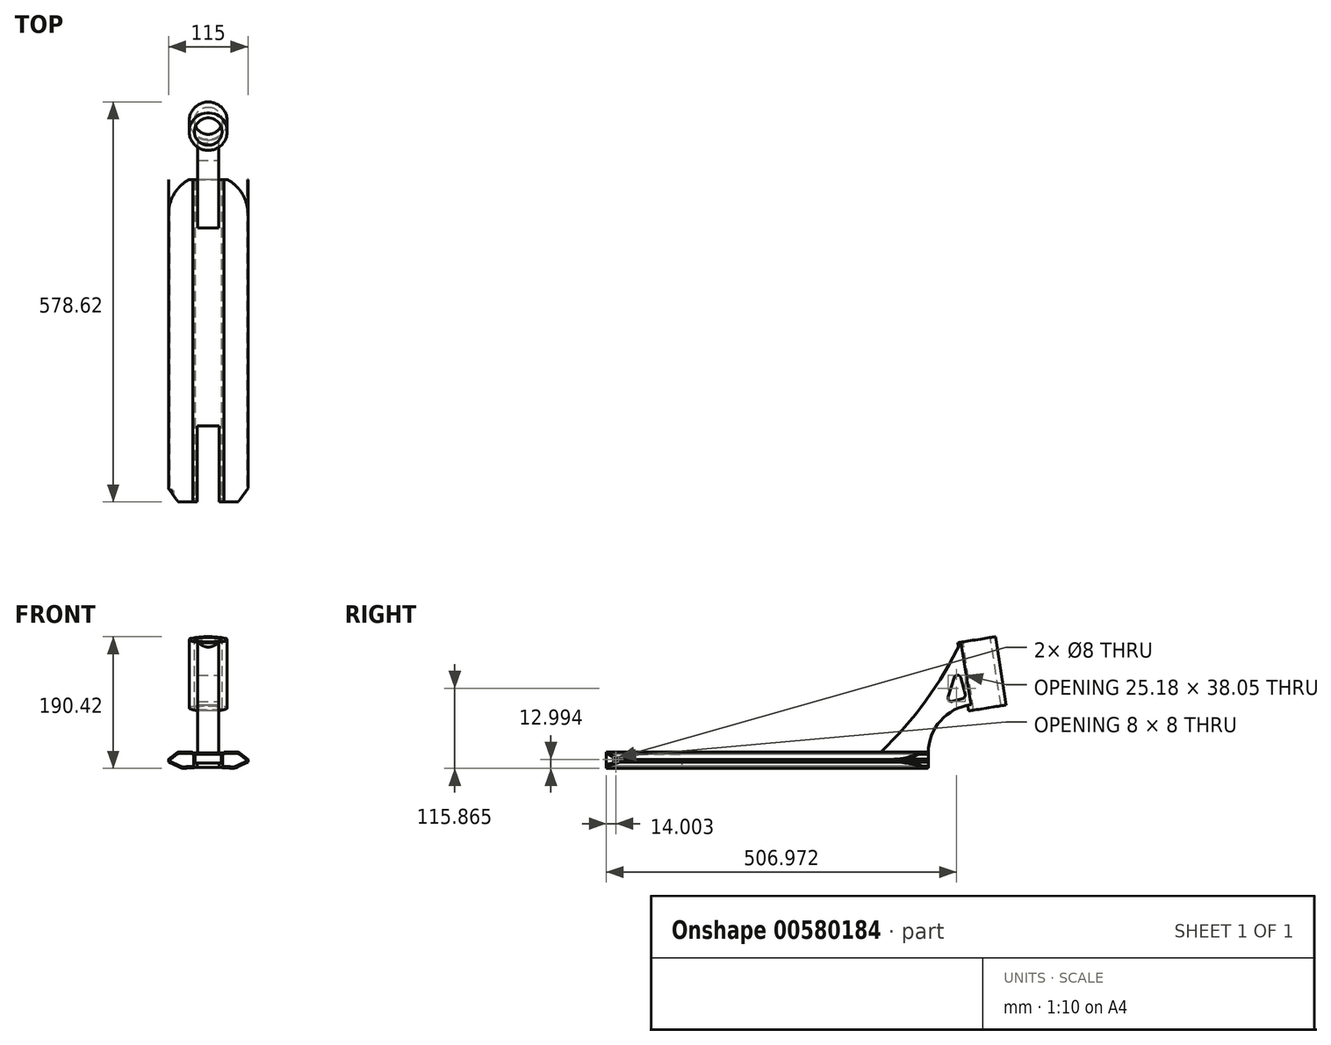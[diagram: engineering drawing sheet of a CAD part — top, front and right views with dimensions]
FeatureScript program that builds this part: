
annotation { "Feature Type Name" : "Feature", "Feature Type Description" : "" }
export const myFeature = defineFeature(function(context is Context, id is Id, definition is map)
    precondition{}
    {
        {
            var Q0;
            Q0=qCreatedBy(makeId("Front.planeOp"),FACE);
            var sketch = newSketch(context, id + "F0", { "sketchPlane" : qUnion([Q0])});
            skLineSegment(sketch, "E0", {"start": v(0, 0) * mm, "end": v(0, 62.93) * mm, "construction": true});
            skLineSegment(sketch, "E1", {"start": v(0, 21.56) * mm, "end": v(22.5, 21.56) * mm});
            skLineSegment(sketch, "E2", {"start": v(22.5, 21.56) * mm, "end": v(22.5, 22.86) * mm});
            skLineSegment(sketch, "E3", {"start": v(22.5, 22.86) * mm, "end": v(43.82, 22.86) * mm});
            skLineSegment(sketch, "E4", {"start": v(43.82, 22.86) * mm, "end": v(57.5, 12.15) * mm});
            skLineSegment(sketch, "E5", {"start": v(57.5, 12.15) * mm, "end": v(57.5, 8.15) * mm});
            skLineSegment(sketch, "E6", {"start": v(57.5, 8.15) * mm, "end": v(37.5, -1.14) * mm});
            skLineSegment(sketch, "E7.MirrorCS", {"start": v(0, 21.56) * mm, "end": v(-22.5, 21.56) * mm});
            skLineSegment(sketch, "E8.MirrorCS", {"start": v(-22.5, 21.56) * mm, "end": v(-22.5, 22.86) * mm});
            skLineSegment(sketch, "E9.MirrorCS", {"start": v(-22.5, 22.86) * mm, "end": v(-43.82, 22.86) * mm});
            skLineSegment(sketch, "E10.MirrorCS", {"start": v(-43.82, 22.86) * mm, "end": v(-57.5, 12.15) * mm});
            skLineSegment(sketch, "E11.MirrorCS", {"start": v(-57.5, 8.15) * mm, "end": v(-37.5, -1.14) * mm});
            skLineSegment(sketch, "E12.MirrorCS", {"start": v(-57.5, 12.15) * mm, "end": v(-57.5, 8.15) * mm});
            skArc(sketch, "E13", {"start": v(37.5, -1.14) * mm, "mid": v(0, 0.56) * mm, "end": v(-37.5, -1.14) * mm});
            skSolve(sketch);
        }
        {
            var Q0;
            Q0 = qSketchRegion(id + "F0", true);
            extrude(context, id + "F1", {"entities" : qUnion([Q0]), "endBound" : BoundingType.SYMMETRIC, "depth" : 500 * mm, "offsetDistance" : 25 * mm});
        }
        {
            var Q0;
            Q0=qCreatedBy(makeId("Front.planeOp"),FACE);
            var sketch = newSketch(context, id + "F2", { "sketchPlane" : qUnion([Q0])});
            skLineSegment(sketch, "E14.bottom", {"start": v(-19, 19.56) * mm, "end": v(19, 19.56) * mm});
            skLineSegment(sketch, "E14.top", {"start": v(-19, 6.56) * mm, "end": v(19, 6.56) * mm});
            skLineSegment(sketch, "E14.left", {"start": v(-19, 19.56) * mm, "end": v(-19, 6.56) * mm});
            skLineSegment(sketch, "E14.right", {"start": v(19, 19.56) * mm, "end": v(19, 6.56) * mm});
            skSolve(sketch);
        }
        {
            var Q0;
            Q0 = qSketchRegion(id + "F2", true);
            extrude(context, id + "F3", {"entities" : qUnion([Q0]), "operationType" : NewBodyOperationType.REMOVE, "endBound" : BoundingType.SYMMETRIC, "oppositeDirection" : true, "depth" : 500 * mm, "offsetDistance" : 25 * mm});
        }
        {
            var Q0;
            Q0=makeQuery(id+"F1.opExtrude","SWEPT_EDGE",EDGE,{"disambiguationData":[OSD([sQuery(id+"F0.wireOp",EDGE,"E8.MirrorCS"),sQuery(id+"F0.wireOp",EDGE,"E9.MirrorCS")])]});
            var Q1;
            Q1=makeQuery(id+"F1.opExtrude","SWEPT_EDGE",EDGE,{"disambiguationData":[OSD([sQuery(id+"F0.wireOp",EDGE,"E2"),sQuery(id+"F0.wireOp",EDGE,"E3")])]});
            fillet(context, id + "F4", {"entities" : qUnion([Q0, Q1]), "radius" : 2 * mm, "tangentPropagation" : true, "allowEdgeOverflow" : false});
        }
        {
            var Q0;
            Q0=makeQuery(id+"F1.opExtrude","SWEPT_EDGE",EDGE,{"disambiguationData":[OSD([sQuery(id+"F0.wireOp",EDGE,"E3"),sQuery(id+"F0.wireOp",EDGE,"E4")])]});
            var Q1;
            Q1=makeQuery(id+"F1.opExtrude","SWEPT_EDGE",EDGE,{"disambiguationData":[OSD([sQuery(id+"F0.wireOp",EDGE,"E9.MirrorCS"),sQuery(id+"F0.wireOp",EDGE,"E10.MirrorCS")])]});
            var Q2;
            Q2=makeQuery(id+"F1.opExtrude","SWEPT_EDGE",EDGE,{"disambiguationData":[OSD([sQuery(id+"F0.wireOp",EDGE,"E11.MirrorCS"),sQuery(id+"F0.wireOp",EDGE,"E13")])]});
            var Q3;
            Q3=makeQuery(id+"F1.opExtrude","SWEPT_EDGE",EDGE,{"disambiguationData":[OSD([sQuery(id+"F0.wireOp",EDGE,"E6"),sQuery(id+"F0.wireOp",EDGE,"E13")])]});
            fillet(context, id + "F5", {"entities" : qUnion([Q0, Q1, Q2, Q3]), "radius" : 9 * mm, "tangentPropagation" : true, "allowEdgeOverflow" : false});
        }
        {
            var Q0;
            Q0=makeQuery(id+"F1.opExtrude","CAP_FACE",FACE,{"disambiguationData":[OSD([sQuery(id+"F0.wireOp",EDGE,"E1"),sQuery(id+"F0.wireOp",EDGE,"E2"),sQuery(id+"F0.wireOp",EDGE,"E3"),sQuery(id+"F0.wireOp",EDGE,"E4"),sQuery(id+"F0.wireOp",EDGE,"E5"),sQuery(id+"F0.wireOp",EDGE,"E6"),sQuery(id+"F0.wireOp",EDGE,"E7.MirrorCS"),sQuery(id+"F0.wireOp",EDGE,"E8.MirrorCS"),sQuery(id+"F0.wireOp",EDGE,"E9.MirrorCS"),sQuery(id+"F0.wireOp",EDGE,"E10.MirrorCS"),sQuery(id+"F0.wireOp",EDGE,"E11.MirrorCS"),sQuery(id+"F0.wireOp",EDGE,"E12.MirrorCS"),sQuery(id+"F0.wireOp",EDGE,"E13")])],"isStart":false});
            var sketch = newSketch(context, id + "F6", { "sketchPlane" : qUnion([Q0])});
            skLineSegment(sketch, "E15.0.0", {"start": v(-57.5, 8.15) * mm, "end": v(-39.68, -0.12) * mm});
            skArc(sketch, "E15.0.1", {"start": v(-39.68, -0.12) * mm, "mid": v(-37.46, -0.82) * mm, "end": v(-35.13, -0.93) * mm});
            skArc(sketch, "E15.0.2", {"start": v(-35.13, -0.93) * mm, "mid": v(0, 0.56) * mm, "end": v(35.13, -0.93) * mm});
            skArc(sketch, "E15.0.3", {"start": v(35.13, -0.93) * mm, "mid": v(37.46, -0.82) * mm, "end": v(39.68, -0.12) * mm});
            skLineSegment(sketch, "E15.0.4", {"start": v(39.68, -0.12) * mm, "end": v(57.5, 8.15) * mm});
            skLineSegment(sketch, "E15.0.5", {"start": v(57.5, 8.15) * mm, "end": v(57.5, 12.15) * mm});
            skLineSegment(sketch, "E15.0.6", {"start": v(57.5, 12.15) * mm, "end": v(46.27, 20.95) * mm});
            skArc(sketch, "E15.0.7", {"start": v(46.27, 20.95) * mm, "mid": v(43.65, 22.37) * mm, "end": v(40.72, 22.86) * mm});
            skLineSegment(sketch, "E15.0.8", {"start": v(40.72, 22.86) * mm, "end": v(24.37, 22.86) * mm});
            skArc(sketch, "E15.0.9", {"start": v(24.37, 22.86) * mm, "mid": v(23.23, 22.5) * mm, "end": v(22.5, 21.56) * mm});
            skLineSegment(sketch, "E15.0.10", {"start": v(22.5, 21.56) * mm, "end": v(-22.5, 21.56) * mm});
            skArc(sketch, "E15.0.11", {"start": v(-22.5, 21.56) * mm, "mid": v(-23.23, 22.5) * mm, "end": v(-24.37, 22.86) * mm});
            skLineSegment(sketch, "E15.0.12", {"start": v(-24.37, 22.86) * mm, "end": v(-40.72, 22.86) * mm});
            skArc(sketch, "E15.0.13", {"start": v(-40.72, 22.86) * mm, "mid": v(-43.65, 22.37) * mm, "end": v(-46.27, 20.95) * mm});
            skLineSegment(sketch, "E15.0.14", {"start": v(-46.27, 20.95) * mm, "end": v(-57.5, 12.15) * mm});
            skLineSegment(sketch, "E15.0.15", {"start": v(-57.5, 12.15) * mm, "end": v(-57.5, 8.15) * mm});
            skArc(sketch, "E16.0", {"start": v(-35.3, 1.07) * mm, "mid": v(0, 2.56) * mm, "end": v(35.3, 1.07) * mm});
            skArc(sketch, "E16.1", {"start": v(-38.84, 1.7) * mm, "mid": v(-37.1, 1.15) * mm, "end": v(-35.3, 1.07) * mm});
            skLineSegment(sketch, "E16.2", {"start": v(-24.87, 20.86) * mm, "end": v(-40.72, 20.86) * mm});
            skArc(sketch, "E16.3", {"start": v(-40.72, 20.86) * mm, "mid": v(-43, 20.48) * mm, "end": v(-45.03, 19.38) * mm});
            skLineSegment(sketch, "E16.4", {"start": v(-45.03, 19.38) * mm, "end": v(-55.62, 11.09) * mm});
            skLineSegment(sketch, "E16.5", {"start": v(-55.42, 9.4) * mm, "end": v(-38.84, 1.7) * mm});
            skPoint(sketch, "E17.visualSharp", {"position": v(-56.9, 10.08) * mm});
            skArc(sketch, "E17.filletArc", {"start": v(-55.62, 11.09) * mm, "mid": v(-56, 10.18) * mm, "end": v(-55.42, 9.4) * mm});
            skLineSegment(sketch, "E18", {"start": v(-21, 2.03) * mm, "end": v(-21, 19.56) * mm});
            skLineSegment(sketch, "E19", {"start": v(-21, 19.56) * mm, "end": v(-23, 19.56) * mm});
            skPoint(sketch, "E20.visualSharp", {"position": v(-26.02, 20.86) * mm});
            skArc(sketch, "E20.filletArc", {"start": v(-23, 19.56) * mm, "mid": v(-23.73, 20.5) * mm, "end": v(-24.87, 20.86) * mm});
            skLineSegment(sketch, "E21.MirrorCS", {"start": v(21, 2.03) * mm, "end": v(21, 19.56) * mm});
            skLineSegment(sketch, "E22.MirrorCS", {"start": v(21, 19.56) * mm, "end": v(23, 19.56) * mm});
            skArc(sketch, "E23.MirrorCS", {"start": v(23, 19.56) * mm, "mid": v(23.73, 20.5) * mm, "end": v(24.87, 20.86) * mm});
            skLineSegment(sketch, "E24.MirrorCS", {"start": v(24.87, 20.86) * mm, "end": v(40.72, 20.86) * mm});
            skArc(sketch, "E25.MirrorCS", {"start": v(40.72, 20.86) * mm, "mid": v(43, 20.48) * mm, "end": v(45.03, 19.38) * mm});
            skLineSegment(sketch, "E26.MirrorCS", {"start": v(45.03, 19.38) * mm, "end": v(55.62, 11.09) * mm});
            skArc(sketch, "E27.MirrorCS", {"start": v(55.62, 11.09) * mm, "mid": v(56, 10.18) * mm, "end": v(55.42, 9.4) * mm});
            skLineSegment(sketch, "E28.MirrorCS", {"start": v(55.42, 9.4) * mm, "end": v(38.84, 1.7) * mm});
            skArc(sketch, "E29.MirrorCS", {"start": v(38.84, 1.7) * mm, "mid": v(37.1, 1.15) * mm, "end": v(35.3, 1.07) * mm});
            skSolve(sketch);
        }
        {
            var Q0;
            {var subQ0=sQuery(id+"F6.wireOp",EDGE,"E16.1");Q0=makeQuery(id+"F6.imprint","IMPRINT",FACE,{"disambiguationData":[TD([[makeQuery(id+"F6.imprint","IMPRINT",EDGE,{"derivedFrom":subQ0}),1.0]])]});}
            var Q1;
            {var subQ2=sQuery(id+"F6.wireOp",EDGE,"E21.MirrorCS");Q1=makeQuery(id+"F6.imprint","IMPRINT",FACE,{"disambiguationData":[TD([[makeQuery(id+"F6.imprint","IMPRINT",EDGE,{"derivedFrom":subQ2}),-1.0]])]});}
            extrude(context, id + "F7", {"entities" : qUnion([Q0, Q1]), "operationType" : NewBodyOperationType.REMOVE, "endBound" : BoundingType.THROUGH_ALL, "oppositeDirection" : true, "depth" : 25 * mm, "offsetDistance" : 25 * mm});
        }
        {
            var Q0;
            Q0=qCreatedBy(makeId("Top.planeOp"),FACE);
            var sketch = newSketch(context, id + "F8", { "sketchPlane" : qUnion([Q0])});
            skArc(sketch, "E30", {"start": v(57.5, 200.38) * mm, "mid": v(0, 257.5) * mm, "end": v(-57.5, 200.38) * mm});
            skLineSegment(sketch, "E31", {"start": v(-57.5, 200.38) * mm, "end": v(-56.97, 280.38) * mm});
            skLineSegment(sketch, "E32", {"start": v(57.5, 200.38) * mm, "end": v(56.97, 280.38) * mm});
            skLineSegment(sketch, "E33", {"start": v(56.97, 280.38) * mm, "end": v(-56.97, 280.38) * mm});
            skSolve(sketch);
        }
        {
            var Q0;
            Q0 = qSketchRegion(id + "F8", true);
            extrude(context, id + "F9", {"entities" : qUnion([Q0]), "operationType" : NewBodyOperationType.REMOVE, "endBound" : BoundingType.THROUGH_ALL, "oppositeDirection" : true, "depth" : 25 * mm, "offsetDistance" : 25 * mm, "hasSecondDirection" : true, "secondDirectionBound" : SecondDirectionBoundingType.THROUGH_ALL, "secondDirectionOppositeDirection" : false, "secondDirectionDepth" : 25 * mm});
        }
        {
            var Q0;
            Q0=qCreatedBy(makeId("Top.planeOp"),FACE);
            var sketch = newSketch(context, id + "F10", { "sketchPlane" : qUnion([Q0])});
            skLineSegment(sketch, "E34", {"start": v(-43.3, -216.07) * mm, "end": v(-16, -216.07) * mm});
            skLineSegment(sketch, "E35", {"start": v(-16, -216.07) * mm, "end": v(-16, -106.07) * mm});
            skLineSegment(sketch, "E36", {"start": v(-16, -106.07) * mm, "end": v(16, -106.07) * mm});
            skLineSegment(sketch, "E37", {"start": v(16, -106.07) * mm, "end": v(16, -216.07) * mm});
            skLineSegment(sketch, "E38", {"start": v(16, -216.07) * mm, "end": v(43.3, -216.07) * mm});
            skLineSegment(sketch, "E39", {"start": v(43.3, -216.07) * mm, "end": v(68, -182.07) * mm});
            skLineSegment(sketch, "E40", {"start": v(68, -182.07) * mm, "end": v(68, -312.07) * mm});
            skLineSegment(sketch, "E41", {"start": v(68, -312.07) * mm, "end": v(-68, -312.07) * mm});
            skLineSegment(sketch, "E42", {"start": v(-68, -312.07) * mm, "end": v(-68, -182.07) * mm});
            skLineSegment(sketch, "E43", {"start": v(-68, -182.07) * mm, "end": v(-43.3, -216.07) * mm});
            skLineSegment(sketch, "E44", {"start": v(0, 0) * mm, "end": v(0, -312.07) * mm});
            skPoint(sketch, "E44.endSnap0", {"position": v(0, -312.07) * mm});
            skSolve(sketch);
        }
        {
            var Q0;
            Q0 = qSketchRegion(id + "F10", true);
            extrude(context, id + "F11", {"entities" : qUnion([Q0]), "operationType" : NewBodyOperationType.REMOVE, "endBound" : BoundingType.THROUGH_ALL, "oppositeDirection" : true, "depth" : 25 * mm, "offsetDistance" : 25 * mm, "hasSecondDirection" : true, "secondDirectionBound" : SecondDirectionBoundingType.THROUGH_ALL, "secondDirectionOppositeDirection" : false, "secondDirectionDepth" : 25 * mm});
        }
        {
            var Q0;
            Q0=qCreatedBy(makeId("Right.planeOp"),FACE);
            var sketch = newSketch(context, id + "F12", { "sketchPlane" : qUnion([Q0])});
            skLineSegment(sketch, "E45", {"start": v(180, 21.56) * mm, "end": v(250, 21.56) * mm});
            skArc(sketch, "E46", {"start": v(311.37, 91.03) * mm, "mid": v(267.54, 67.9) * mm, "end": v(250, 21.56) * mm});
            skArc(sketch, "E47", {"start": v(180, 21.56) * mm, "mid": v(245.78, 96.25) * mm, "end": v(297.03, 181.56) * mm});
            skLineSegment(sketch, "E48", {"start": v(297.03, 181.56) * mm, "end": v(342.46, 188.76) * mm});
            skLineSegment(sketch, "E49", {"start": v(342.46, 188.76) * mm, "end": v(358.1, 90) * mm});
            skLineSegment(sketch, "E50", {"start": v(358.1, 90) * mm, "end": v(312.67, 82.8) * mm});
            skLineSegment(sketch, "E51", {"start": v(311.37, 91.03) * mm, "end": v(312.67, 82.8) * mm});
            skSolve(sketch);
        }
        {
            var Q0;
            Q0 = qSketchRegion(id + "F12", true);
            extrude(context, id + "F13", {"entities" : qUnion([Q0]), "operationType" : NewBodyOperationType.ADD, "endBound" : BoundingType.SYMMETRIC, "depth" : 30 * mm, "offsetDistance" : 25 * mm});
        }
        {
            var Q0;
            Q0=makeQuery(id+"F13.opExtrude","SWEPT_FACE",FACE,{"disambiguationData":[OSD([sQuery(id+"F12.wireOp",EDGE,"E48")])]});
            var sketch = newSketch(context, id + "F14", { "sketchPlane" : qUnion([Q0])});
            skCircle(sketch, "E52", {"center": v(0, 344.78) * mm, "radius": 27.5 * mm});
            skSolve(sketch);
        }
        {
            var Q0;
            Q0 = qSketchRegion(id + "F14", true);
            var Q1;
            Q1=makeQuery(id+"F13.opExtrude","SWEPT_FACE",FACE,{"disambiguationData":[OSD([sQuery(id+"F12.wireOp",EDGE,"E50")])]});
            extrude(context, id + "F15", {"entities" : qUnion([Q0]), "operationType" : NewBodyOperationType.ADD, "endBound" : BoundingType.UP_TO_SURFACE, "oppositeDirection" : true, "depth" : 26 * mm, "endBoundEntityFace" : qUnion([Q1]), "offsetDistance" : 25 * mm});
        }
        {
            var Q0;
            Q0=makeQuery(id+"F15.boolean.opBoolean","MERGE",FACE,{"derivedFrom":[makeQuery(id+"F13.opExtrude","SWEPT_FACE",FACE,{"disambiguationData":[OSD([sQuery(id+"F12.wireOp",EDGE,"E48")])]}),makeQuery(id+"F15.opExtrude","CAP_FACE",FACE,{"disambiguationData":[OSD([sQuery(id+"F14.wireOp",EDGE,"E52")])],"isStart":true})]});
            var sketch = newSketch(context, id + "F16", { "sketchPlane" : qUnion([Q0])});
            skPoint(sketch, "E53", {"position": v(0, 344.78) * mm});
            skSolve(sketch);
        }
        {
            var Q0;
            Q0=sQuery(id+"F16.wireOp",VERTEX,"E53");
            var Q1;
            Q1=makeQuery(id+"F1.opExtrude","SWEPT_BODY",BODY,{"disambiguationData":[OSD([sQuery(id+"F0.wireOp",EDGE,"E1"),sQuery(id+"F0.wireOp",EDGE,"E2"),sQuery(id+"F0.wireOp",EDGE,"E3"),sQuery(id+"F0.wireOp",EDGE,"E4"),sQuery(id+"F0.wireOp",EDGE,"E5"),sQuery(id+"F0.wireOp",EDGE,"E6"),sQuery(id+"F0.wireOp",EDGE,"E7.MirrorCS"),sQuery(id+"F0.wireOp",EDGE,"E8.MirrorCS"),sQuery(id+"F0.wireOp",EDGE,"E9.MirrorCS"),sQuery(id+"F0.wireOp",EDGE,"E10.MirrorCS"),sQuery(id+"F0.wireOp",EDGE,"E11.MirrorCS"),sQuery(id+"F0.wireOp",EDGE,"E12.MirrorCS"),sQuery(id+"F0.wireOp",EDGE,"E13")])]});
            hole(context, id + "F17", {"style" : HoleStyle.SIMPLE, "endStyle" : HoleEndStyle.THROUGH, "holeDiameter" : 40 * mm, "majorDiameter" : 5 * mm, "isTappedThrough" : true, "tappedDepth" : 12 * mm, "tapClearance" : 3, "locations" : qUnion([Q0]), "scope" : qUnion([Q1])});
        }
        {
            var Q0;
            Q0=makeQuery(id+"F7.boolean.opBoolean","COPY",FACE,{"derivedFrom":makeQuery(id+"F7.opExtrude","SWEPT_FACE",FACE,{"disambiguationData":[OSD([sQuery(id+"F6.wireOp",EDGE,"E21.MirrorCS")])]})});
            var sketch = newSketch(context, id + "F18", { "sketchPlane" : qUnion([Q0])});
            skPoint(sketch, "E54", {"position": v(-202.07, 12.03) * mm});
            skSolve(sketch);
        }
        {
            var Q0;
            Q0=sQuery(id+"F18.wireOp",VERTEX,"E54");
            var Q1;
            Q1=makeQuery(id+"F1.opExtrude","SWEPT_BODY",BODY,{"disambiguationData":[OSD([sQuery(id+"F0.wireOp",EDGE,"E1"),sQuery(id+"F0.wireOp",EDGE,"E2"),sQuery(id+"F0.wireOp",EDGE,"E3"),sQuery(id+"F0.wireOp",EDGE,"E4"),sQuery(id+"F0.wireOp",EDGE,"E5"),sQuery(id+"F0.wireOp",EDGE,"E6"),sQuery(id+"F0.wireOp",EDGE,"E7.MirrorCS"),sQuery(id+"F0.wireOp",EDGE,"E8.MirrorCS"),sQuery(id+"F0.wireOp",EDGE,"E9.MirrorCS"),sQuery(id+"F0.wireOp",EDGE,"E10.MirrorCS"),sQuery(id+"F0.wireOp",EDGE,"E11.MirrorCS"),sQuery(id+"F0.wireOp",EDGE,"E12.MirrorCS"),sQuery(id+"F0.wireOp",EDGE,"E13")])]});
            hole(context, id + "F19", {"style" : HoleStyle.SIMPLE, "endStyle" : HoleEndStyle.THROUGH, "holeDiameter" : 8 * mm, "majorDiameter" : 5 * mm, "isTappedThrough" : true, "tappedDepth" : 12 * mm, "tapClearance" : 3, "locations" : qUnion([Q0]), "scope" : qUnion([Q1])});
        }
        {
            var Q0;
            Q0=makeQuery(id+"F13.opExtrude","CAP_FACE",FACE,{"disambiguationData":[OSD([sQuery(id+"F12.wireOp",EDGE,"E45"),sQuery(id+"F12.wireOp",EDGE,"E46"),sQuery(id+"F12.wireOp",EDGE,"E47"),sQuery(id+"F12.wireOp",EDGE,"E48"),sQuery(id+"F12.wireOp",EDGE,"E49"),sQuery(id+"F12.wireOp",EDGE,"E50"),sQuery(id+"F12.wireOp",EDGE,"E51")])],"isStart":false});
            var sketch = newSketch(context, id + "F20", { "sketchPlane" : qUnion([Q0])});
            skLineSegment(sketch, "E55", {"start": v(296.87, 130.24) * mm, "end": v(303.33, 106.54) * mm});
            skLineSegment(sketch, "E56", {"start": v(299.88, 100.41) * mm, "end": v(284.68, 96.07) * mm});
            skLineSegment(sketch, "E57", {"start": v(278.54, 102.37) * mm, "end": v(287.27, 130.42) * mm});
            skLineSegment(sketch, "E58", {"start": v(247, 32.86) * mm, "end": v(262.38, 75.15) * mm});
            skLineSegment(sketch, "E59", {"start": v(255.87, 57.26) * mm, "end": v(248.19, 36.15) * mm});
            skLineSegment(sketch, "E60", {"start": v(243.5, 32.86) * mm, "end": v(226.52, 32.86) * mm});
            skLineSegment(sketch, "E61", {"start": v(223.27, 41.66) * mm, "end": v(247.92, 62.77) * mm});
            skPoint(sketch, "E62.visualSharp", {"position": v(213, 32.86) * mm});
            skArc(sketch, "E62.filletArc", {"start": v(223.27, 41.66) * mm, "mid": v(221.83, 36.13) * mm, "end": v(226.52, 32.86) * mm});
            skPoint(sketch, "E63.visualSharp", {"position": v(262.38, 75.15) * mm});
            skArc(sketch, "E63.filletArc", {"start": v(255.87, 57.26) * mm, "mid": v(254.02, 63.08) * mm, "end": v(247.92, 62.77) * mm});
            skPoint(sketch, "E64.visualSharp", {"position": v(292.37, 146.77) * mm});
            skArc(sketch, "E64.filletArc", {"start": v(296.87, 130.24) * mm, "mid": v(292.14, 133.93) * mm, "end": v(287.27, 130.42) * mm});
            skPoint(sketch, "E65.visualSharp", {"position": v(304.63, 101.77) * mm});
            skArc(sketch, "E65.filletArc", {"start": v(299.88, 100.41) * mm, "mid": v(302.86, 102.77) * mm, "end": v(303.33, 106.54) * mm});
            skPoint(sketch, "E66.visualSharp", {"position": v(275.78, 93.53) * mm});
            skArc(sketch, "E66.filletArc", {"start": v(278.54, 102.37) * mm, "mid": v(279.73, 97.39) * mm, "end": v(284.68, 96.07) * mm});
            skPoint(sketch, "E67.visualSharp", {"position": v(247, 32.86) * mm});
            skArc(sketch, "E67.filletArc", {"start": v(243.5, 32.86) * mm, "mid": v(246.36, 33.77) * mm, "end": v(248.19, 36.15) * mm});
            skSolve(sketch);
        }
        {
            var Q0;
            Q0=makeQuery(id+"F20.imprint","IMPRINT",FACE,{"disambiguationData":[TD([[makeQuery(id+"F20.imprint","IMPRINT",EDGE,{"derivedFrom":sQuery(id+"F20.wireOp",EDGE,"E55")}),-1.0]])]});
            var Q1;
            Q1=makeQuery(id+"F20.imprint","IMPRINT",FACE,{"disambiguationData":[TD([[makeQuery(id+"F20.imprint","IMPRINT",EDGE,{"derivedFrom":sQuery(id+"F20.wireOp",EDGE,"E59")}),-1.0]])]});
            extrude(context, id + "F21", {"entities" : qUnion([Q0, Q1]), "operationType" : NewBodyOperationType.REMOVE, "endBound" : BoundingType.THROUGH_ALL, "oppositeDirection" : true, "depth" : 25 * mm, "offsetDistance" : 25 * mm});
        }
    });
